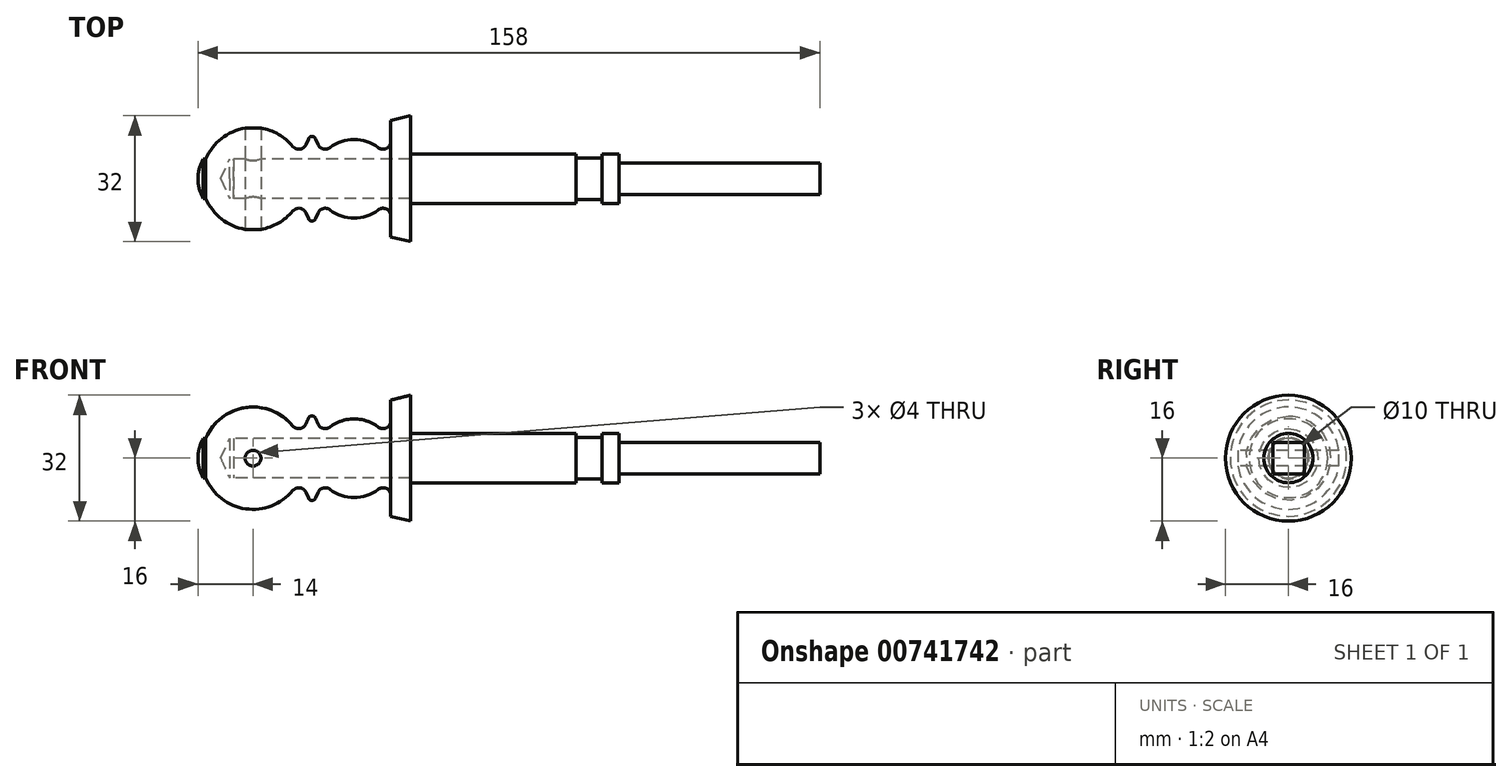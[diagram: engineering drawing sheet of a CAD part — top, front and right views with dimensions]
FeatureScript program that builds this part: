
annotation { "Feature Type Name" : "Feature", "Feature Type Description" : "" }
export const myFeature = defineFeature(function(context is Context, id is Id, definition is map)
    precondition{}
    {
        {
            var Q0;
            Q0=qCreatedBy(makeId("Front.planeOp"),FACE);
            var sketch = newSketch(context, id + "F0", { "sketchPlane" : qUnion([Q0])});
            skLineSegment(sketch, "E0", {"start": v(0, 0) * mm, "end": v(0, 6.25) * mm});
            skLineSegment(sketch, "E1", {"start": v(0, 6.25) * mm, "end": v(42, 6.25) * mm});
            skLineSegment(sketch, "E2", {"start": v(42, 6.25) * mm, "end": v(42, 5.25) * mm});
            skLineSegment(sketch, "E3", {"start": v(42, 5.25) * mm, "end": v(48.7, 5.25) * mm});
            skLineSegment(sketch, "E4", {"start": v(48.7, 5.25) * mm, "end": v(48.7, 6.25) * mm});
            skLineSegment(sketch, "E5", {"start": v(48.7, 6.25) * mm, "end": v(53, 6.25) * mm});
            skLineSegment(sketch, "E6", {"start": v(53, 6.25) * mm, "end": v(53, 0) * mm});
            skLineSegment(sketch, "E7", {"start": v(53, 0) * mm, "end": v(0, 0) * mm});
            skLineSegment(sketch, "E8", {"start": v(-8.02, 0) * mm, "end": v(60.62, 0) * mm, "construction": true});
            skSolve(sketch);
        }
        {
            var Q0;
            Q0=makeQuery(id+"F0.imprint","IMPRINT",FACE,{"disambiguationData":[TD([[makeQuery(id+"F0.imprint","IMPRINT",EDGE,{"derivedFrom":sQuery(id+"F0.wireOp",EDGE,"E0")}),-1.0]])]});
            var Q1;
            Q1=sQuery(id+"F0.wireOp",EDGE,"E8");
            revolve(context, id + "F1", {"surfaceOperationType" : NewSurfaceOperationType.NEW, "entities" : qUnion([Q0]), "axis" : qUnion([Q1]), "revolveType" : RevolveType.FULL});
        }
        {
            var Q0;
            Q0=makeQuery(id+"F1.opRevolve","SWEPT_FACE",FACE,{"disambiguationData":[OSD([sQuery(id+"F0.wireOp",EDGE,"E6")])]});
            var sketch = newSketch(context, id + "F2", { "sketchPlane" : qUnion([Q0])});
            skLineSegment(sketch, "E9", {"start": v(0, 10.14) * mm, "end": v(0, -9.87) * mm, "construction": true});
            skLineSegment(sketch, "E10", {"start": v(-10.73, 0) * mm, "end": v(10.24, 0) * mm, "construction": true});
            skLineSegment(sketch, "E11.bottom", {"start": v(-4, 4) * mm, "end": v(4, 4) * mm});
            skLineSegment(sketch, "E11.top", {"start": v(-4, -4) * mm, "end": v(4, -4) * mm});
            skLineSegment(sketch, "E11.left", {"start": v(-4, 4) * mm, "end": v(-4, -4) * mm});
            skLineSegment(sketch, "E11.right", {"start": v(4, 4) * mm, "end": v(4, -4) * mm});
            skSolve(sketch);
        }
        {
            var Q0;
            Q0=makeQuery(id+"F2.imprint","IMPRINT",FACE,{"disambiguationData":[TD([[makeQuery(id+"F2.imprint","IMPRINT",EDGE,{"derivedFrom":sQuery(id+"F2.wireOp",EDGE,"E11.bottom")}),-1.0]])]});
            extrude(context, id + "F3", {"entities" : qUnion([Q0]), "operationType" : NewBodyOperationType.ADD, "depth" : 51 * mm, "offsetDistance" : 25 * mm});
        }
        {
            var Q0;
            Q0=qCreatedBy(makeId("Front.planeOp"),FACE);
            var sketch = newSketch(context, id + "F4", { "sketchPlane" : qUnion([Q0])});
            skLineSegment(sketch, "E12", {"start": v(0, 0) * mm, "end": v(0, 5) * mm});
            skLineSegment(sketch, "E13", {"start": v(0, 5) * mm, "end": v(-45, 5) * mm});
            skLineSegment(sketch, "E14", {"start": v(0, 0) * mm, "end": v(-45, 0) * mm});
            skLineSegment(sketch, "E15", {"start": v(-45, 5) * mm, "end": v(-45, 0) * mm});
            skLineSegment(sketch, "E16.trimOffspring", {"start": v(-45, 0) * mm, "end": v(4.03, 0) * mm, "construction": true});
            skSolve(sketch);
        }
        {
            var Q0;
            Q0=makeQuery(id+"F4.imprint","IMPRINT",FACE,{"disambiguationData":[TD([[makeQuery(id+"F4.imprint","IMPRINT",EDGE,{"derivedFrom":sQuery(id+"F4.wireOp",EDGE,"E12")}),1.0]])]});
            var Q1;
            Q1=sQuery(id+"F4.wireOp",EDGE,"E16.trimOffspring");
            revolve(context, id + "F5", {"operationType" : NewBodyOperationType.ADD, "surfaceOperationType" : NewSurfaceOperationType.NEW, "entities" : qUnion([Q0]), "axis" : qUnion([Q1]), "revolveType" : RevolveType.FULL});
        }
        {
            var Q0;
            Q0=qCreatedBy(makeId("Front.planeOp"),FACE);
            var sketch = newSketch(context, id + "F6", { "sketchPlane" : qUnion([Q0])});
            skLineSegment(sketch, "E17", {"start": v(-58.23, 0) * mm, "end": v(9.35, 0) * mm, "construction": true});
            skLineSegment(sketch, "E18", {"start": v(0, 5) * mm, "end": v(0, 16) * mm});
            skLineSegment(sketch, "E19", {"start": v(0, 16) * mm, "end": v(-5, 14.76) * mm});
            skLineSegment(sketch, "E20", {"start": v(-5, 14.76) * mm, "end": v(-5, 9.5) * mm});
            skLineSegment(sketch, "E21", {"start": v(-46, 5) * mm, "end": v(0, 5) * mm});
            skArc(sketch, "E22", {"start": v(-8.22, 7.92) * mm, "mid": v(-14.33, 10) * mm, "end": v(-20.44, 7.92) * mm});
            skArc(sketch, "E23", {"start": v(-52, 5) * mm, "mid": v(-41.89, 12.86) * mm, "end": v(-29.94, 8.23) * mm});
            skArc(sketch, "E24.filletArc", {"start": v(-8.22, 7.92) * mm, "mid": v(-6.12, 7.7) * mm, "end": v(-5, 9.5) * mm});
            skLineSegment(sketch, "E25", {"start": v(-23.5, 8.72) * mm, "end": v(-24.1, 10.14) * mm});
            skLineSegment(sketch, "E26", {"start": v(-25.95, 10.14) * mm, "end": v(-26.55, 8.72) * mm});
            skArc(sketch, "E27.filletArc", {"start": v(-23.5, 8.72) * mm, "mid": v(-22.17, 7.57) * mm, "end": v(-20.44, 7.92) * mm});
            skArc(sketch, "E28.filletArc", {"start": v(-29.94, 8.23) * mm, "mid": v(-28.1, 7.52) * mm, "end": v(-26.55, 8.72) * mm});
            skArc(sketch, "E29.filletArc", {"start": v(-24.1, 10.14) * mm, "mid": v(-25.03, 10.75) * mm, "end": v(-25.95, 10.14) * mm});
            skLineSegment(sketch, "E30", {"start": v(-28.4, 9.5) * mm, "end": v(-25.03, 9.75) * mm, "construction": true});
            skLineSegment(sketch, "E31", {"start": v(-21.66, 9.5) * mm, "end": v(-25.03, 9.75) * mm, "construction": true});
            skLineSegment(sketch, "E32", {"start": v(-52, 5) * mm, "end": v(-52.66, 5) * mm});
            skLineSegment(sketch, "E33", {"start": v(-54, 0) * mm, "end": v(-48.23, 0) * mm});
            skLineSegment(sketch, "E34", {"start": v(-48.23, 0) * mm, "end": v(-46, 5) * mm});
            skArc(sketch, "E35", {"start": v(-52.66, 5) * mm, "mid": v(-53.66, 2.59) * mm, "end": v(-54, 0) * mm});
            skSolve(sketch);
        }
        {
            var Q0;
            Q0=makeQuery(id+"F6.imprint","IMPRINT",FACE,{"disambiguationData":[TD([[makeQuery(id+"F6.imprint","IMPRINT",EDGE,{"derivedFrom":sQuery(id+"F6.wireOp",EDGE,"E18")}),1.0]])]});
            var Q1;
            Q1=sQuery(id+"F6.wireOp",EDGE,"E17");
            revolve(context, id + "F7", {"surfaceOperationType" : NewSurfaceOperationType.NEW, "entities" : qUnion([Q0]), "axis" : qUnion([Q1]), "revolveType" : RevolveType.FULL});
        }
        {
            var Q0;
            Q0=qCreatedBy(makeId("Front.planeOp"),FACE);
            var sketch = newSketch(context, id + "F8", { "sketchPlane" : qUnion([Q0])});
            skCircle(sketch, "E36", {"center": v(-40, 0) * mm, "radius": 2 * mm});
            skArc(sketch, "E37", {"start": v(-30.18, 8.52) * mm, "mid": v(-53, 0) * mm, "end": v(-30.18, -8.52) * mm, "construction": true});
            skSolve(sketch);
        }
        {
            var Q0;
            Q0 = qSketchRegion(id + "F8", true);
            extrude(context, id + "F9", {"entities" : qUnion([Q0]), "operationType" : NewBodyOperationType.REMOVE, "endBound" : BoundingType.THROUGH_ALL, "oppositeDirection" : true, "depth" : 25 * mm, "offsetDistance" : 25 * mm, "hasSecondDirection" : true, "secondDirectionBound" : SecondDirectionBoundingType.THROUGH_ALL, "secondDirectionOppositeDirection" : false, "secondDirectionDepth" : 25 * mm});
        }
    });
